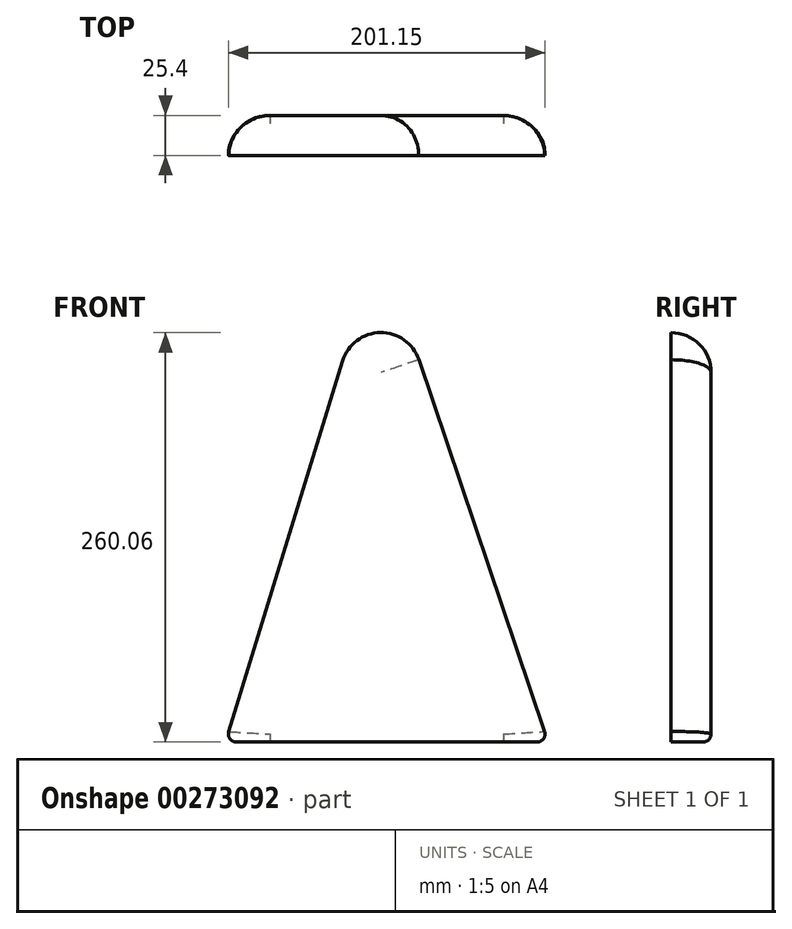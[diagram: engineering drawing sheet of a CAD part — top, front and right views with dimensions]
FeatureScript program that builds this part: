
annotation { "Feature Type Name" : "Feature", "Feature Type Description" : "" }
export const myFeature = defineFeature(function(context is Context, id is Id, definition is map)
    precondition{}
    {
        {
            var Q0;
            Q0=qCreatedBy(makeId("Front.planeOp"),FACE);
            var sketch = newSketch(context, id + "F0", { "sketchPlane" : qUnion([Q0])});
            skLineSegment(sketch, "E0", {"start": v(0, 201.24) * mm, "end": v(-97.5, -116.08) * mm});
            skLineSegment(sketch, "E1", {"start": v(-97.5, -116.08) * mm, "end": v(107.45, -116.08) * mm});
            skLineSegment(sketch, "E2", {"start": v(107.45, -116.08) * mm, "end": v(0, 201.24) * mm});
            skSolve(sketch);
        }
        {
            var Q0;
            Q0 = qSketchRegion(id + "F0", true);
            extrude(context, id + "F1", {"entities" : qUnion([Q0]), "depth" : 25.4 * mm});
        }
        {
            var Q0;
            Q0=makeQuery(id+"F1.opExtrude","CAP_EDGE",EDGE,{"disambiguationData":[OSD([sQuery(id+"F0.wireOp",EDGE,"E2")])],"isStart":true});
            fillet(context, id + "F2", {"entities" : qUnion([Q0]), "radius" : 25.4 * mm, "tangentPropagation" : true, "allowEdgeOverflow" : false});
        }
        {
            var Q0;
            Q0=makeQuery(id+"F1.opExtrude","CAP_EDGE",EDGE,{"disambiguationData":[OSD([sQuery(id+"F0.wireOp",EDGE,"E0")])],"isStart":true});
            fillet(context, id + "F3", {"entities" : qUnion([Q0]), "radius" : 25.4 * mm, "tangentPropagation" : true, "allowEdgeOverflow" : false});
        }
        {
            var Q0;
            Q0=makeQuery(id+"F1.opExtrude","CAP_EDGE",EDGE,{"disambiguationData":[OSD([sQuery(id+"F0.wireOp",EDGE,"E1")])],"isStart":true});
            fillet(context, id + "F4", {"entities" : qUnion([Q0]), "radius" : 5.08 * mm, "tangentPropagation" : true, "allowEdgeOverflow" : false});
        }
    });
